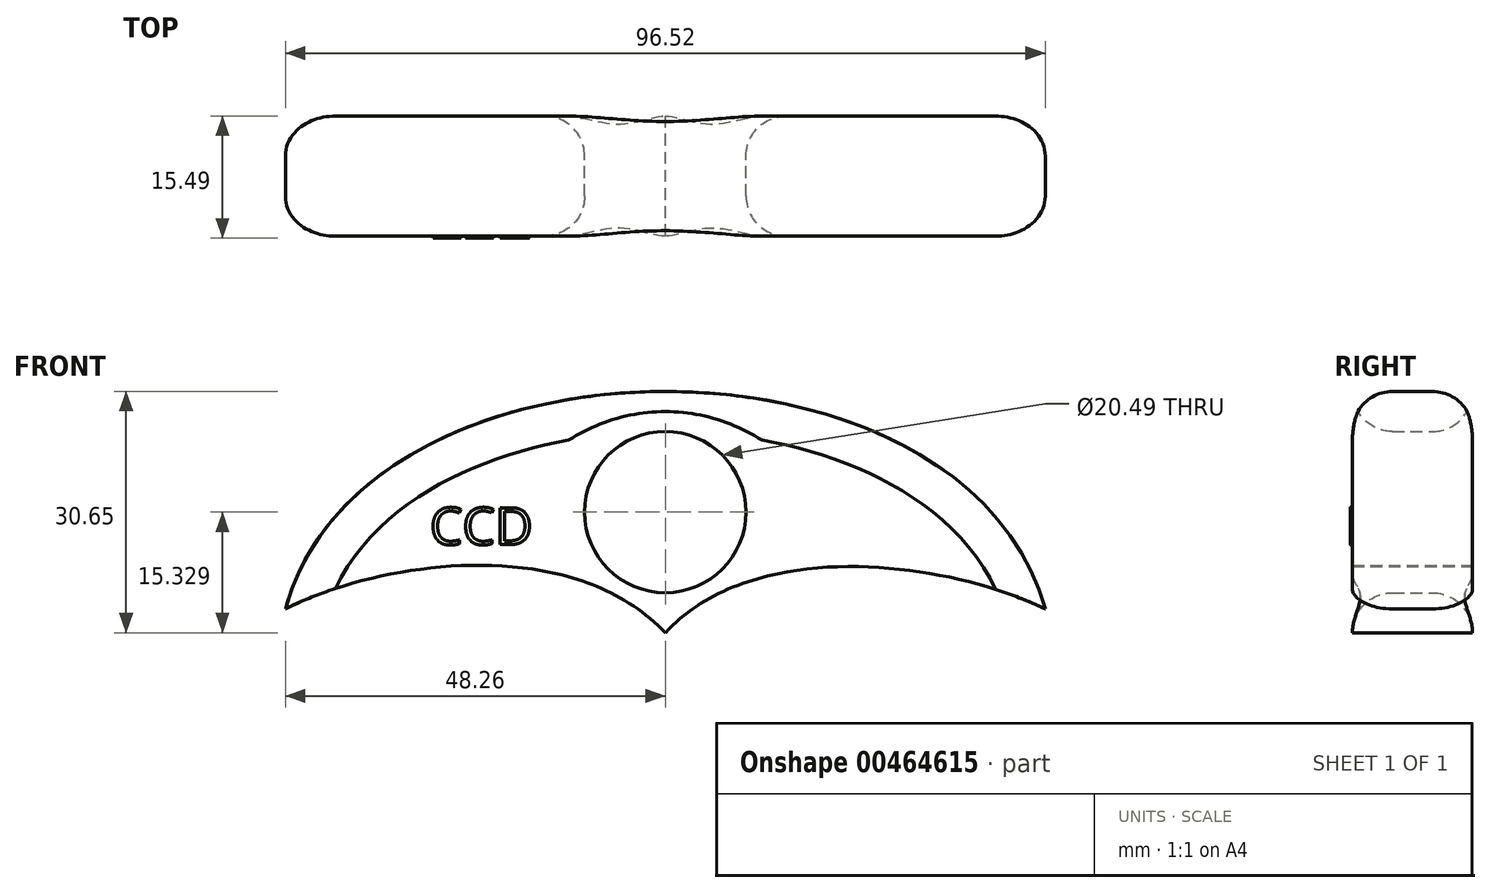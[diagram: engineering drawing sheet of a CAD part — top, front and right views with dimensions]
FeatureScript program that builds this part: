
annotation { "Feature Type Name" : "Feature", "Feature Type Description" : "" }
export const myFeature = defineFeature(function(context is Context, id is Id, definition is map)
    precondition{}
    {
        {
            var Q0;
            Q0=qCreatedBy(makeId("Front.planeOp"),FACE);
            var sketch = newSketch(context, id + "F0", { "sketchPlane" : qUnion([Q0])});
            skPoint(sketch, "E0", {"position": v(0, 0) * mm});
            skPoint(sketch, "E1", {"position": v(48.26, 0) * mm});
            skPoint(sketch, "E2", {"position": v(-48.26, 0) * mm});
            skFitSpline(sketch, "E3", {"points": [v(-48.26, 0) * mm, v(48.26, 0) * mm], "startDerivative": vector(30.48, 110.5) * mm, "endDerivative": vector(30.48, -110.5) * mm});
            skPoint(sketch, "E4", {"position": v(0, -3.03) * mm});
            skFitSpline(sketch, "E5", {"points": [v(-48.26, 0) * mm, v(0, -3.03) * mm], "startDerivative": vector(35.94, 18.1) * mm, "endDerivative": vector(36.46, -38.41) * mm});
            skFitSpline(sketch, "E6", {"points": [v(0, -3.03) * mm, v(48.26, 0) * mm], "startDerivative": vector(34.5, 37.12) * mm, "endDerivative": vector(37.34, -18.1) * mm});
            skLineSegment(sketch, "E7", {"start": v(0, -3.03) * mm, "end": v(0, 27.62) * mm});
            skCircle(sketch, "E8", {"center": v(0, 12.3) * mm, "radius": 10.24 * mm});
            skSolve(sketch);
        }
        {
            var Q0;
            {var subQ5=sQuery(id+"F0.wireOp",EDGE,"E5");Q0=makeQuery(id+"F0.imprint","IMPRINT",FACE,{"disambiguationData":[TD([[makeQuery(id+"F0.imprint","IMPRINT",EDGE,{"derivedFrom":subQ5}),1.0]])]});}
            var Q1;
            {var subQ1=sQuery(id+"F0.wireOp",EDGE,"E6");Q1=makeQuery(id+"F0.imprint","IMPRINT",FACE,{"disambiguationData":[TD([[makeQuery(id+"F0.imprint","IMPRINT",EDGE,{"derivedFrom":subQ1}),1.0]])]});}
            extrude(context, id + "F1", {"entities" : qUnion([Q0, Q1]), "depth" : 15.24 * mm, "symmetric" : true});
        }
        {
            var Q0;
            Q0=makeQuery(id+"F1.opExtrude","CAP_EDGE",EDGE,{"disambiguationData":[OSD([sQuery(id+"F0.wireOp",EDGE,"E8")])],"isStart":false});
            var Q1;
            Q1=makeQuery(id+"F1.opExtrude","CAP_EDGE",EDGE,{"disambiguationData":[OSD([sQuery(id+"F0.wireOp",EDGE,"E8")])],"isStart":true});
            var Q2;
            Q2=makeQuery(id+"F1.opExtrude","CAP_EDGE",EDGE,{"disambiguationData":[OSD([sQuery(id+"F0.wireOp",EDGE,"E3")])],"isStart":false});
            var Q3;
            Q3=makeQuery(id+"F1.opExtrude","CAP_EDGE",EDGE,{"disambiguationData":[OSD([sQuery(id+"F0.wireOp",EDGE,"E3")])],"isStart":true});
            fillet(context, id + "F2", {"entities" : qUnion([Q0, Q1, Q2, Q3]), "radius" : 5.08 * mm, "tangentPropagation" : true, "allowEdgeOverflow" : false});
        }
        {
            var Q0;
            Q0=qCreatedBy(makeId("Front.planeOp"),FACE);
            var sketch = newSketch(context, id + "F3", { "sketchPlane" : qUnion([Q0])});
            skText(sketch, "E9", { "text": "CCD", "fontName": "OpenSans-Regular.ttf"});
            const initialGuessF3  = {"E9": [-0.0299, 0.00818, 1, 0, 0.00472]};
            skSetInitialGuess(sketch, initialGuessF3);
            skSolve(sketch);
        }
        {
            var Q0;
            Q0 = qSketchRegion(id + "F3", true);
            extrude(context, id + "F4", {"entities" : qUnion([Q0]), "operationType" : NewBodyOperationType.ADD, "depth" : 7.87 * mm});
        }
    });
